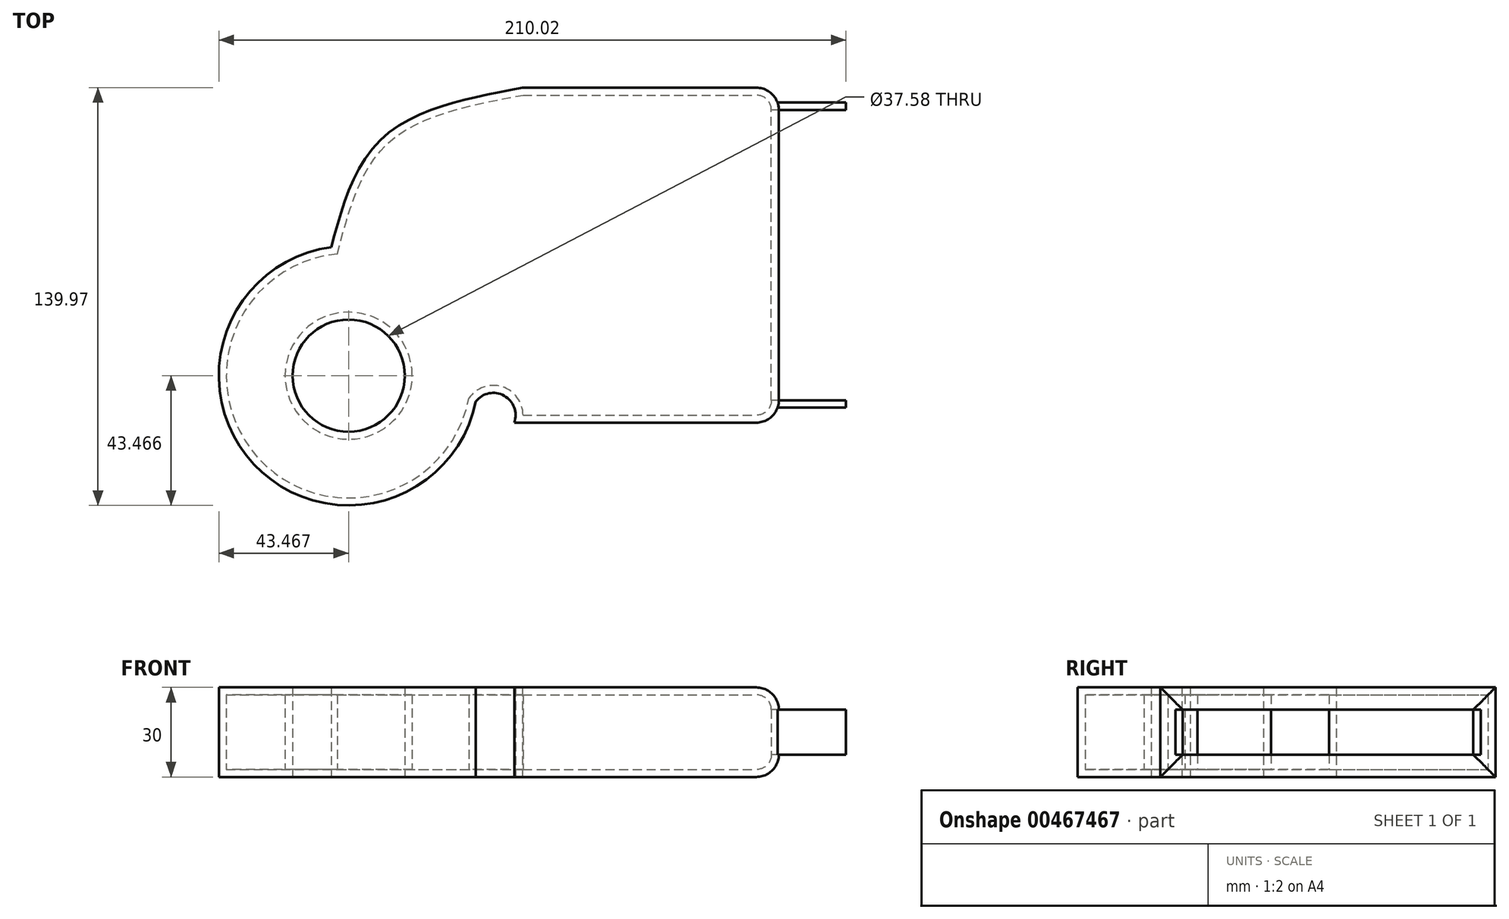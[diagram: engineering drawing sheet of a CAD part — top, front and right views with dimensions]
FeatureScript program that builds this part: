
annotation { "Feature Type Name" : "Feature", "Feature Type Description" : "" }
export const myFeature = defineFeature(function(context is Context, id is Id, definition is map)
    precondition{}
    {
        {
            var Q0;
            Q0=qCreatedBy(makeId("Top.planeOp"),FACE);
            var sketch = newSketch(context, id + "F0", { "sketchPlane" : qUnion([Q0])});
            skLineSegment(sketch, "E0.bottom", {"start": v(-39.88, -54.03) * mm, "end": v(43.27, -54.03) * mm});
            skLineSegment(sketch, "E0.top", {"start": v(-39.88, 53.2) * mm, "end": v(43.27, 53.2) * mm});
            skLineSegment(sketch, "E0.right", {"start": v(43.27, -54.03) * mm, "end": v(43.27, 53.2) * mm});
            skArc(sketch, "E1", {"start": v(-102.06, 0) * mm, "mid": v(-128.58, -68.38) * mm, "end": v(-58.02, -48.36) * mm});
            skArc(sketch, "E2", {"start": v(-39.88, -54.03) * mm, "mid": v(-46.87, -44.53) * mm, "end": v(-58.02, -48.36) * mm});
            skCircle(sketch, "E3", {"center": v(-98.28, -40.8) * mm, "radius": 21.29 * mm});
            skFitSpline(sketch, "E4", {"points": [v(-102.06, 0) * mm, v(-85.1, 37.1) * mm, v(-39.88, 53.2) * mm], "startDerivative": vector(22.98, 88.5) * mm, "endDerivative": vector(100.32, 18.86) * mm});
            skPoint(sketch, "E5", {"position": v(55.98, -27.17) * mm});
            skPoint(sketch, "E6", {"position": v(56.43, 31.28) * mm});
            skSolve(sketch);
        }
        {
            var Q0;
            Q0=makeQuery(id+"F0.imprint","IMPRINT",FACE,{"disambiguationData":[TD([[makeQuery(id+"F0.imprint","IMPRINT",EDGE,{"derivedFrom":sQuery(id+"F0.wireOp",EDGE,"E0.bottom")}),1.0]])]});
            extrude(context, id + "F1", {"entities" : qUnion([Q0]), "depth" : 25 * mm});
        }
        {
            var Q0;
            Q0=makeQuery(id+"F1.opExtrude","SWEPT_FACE",FACE,{"disambiguationData":[OSD([sQuery(id+"F0.wireOp",EDGE,"E0.right")])]});
            fillet(context, id + "F2", {"entities" : qUnion([Q0]), "radius" : 5 * mm, "tangentPropagation" : true, "allowEdgeOverflow" : false});
        }
        {
            var Q0;
            Q0=makeQuery(id+"F1.opExtrude","SWEPT_FACE",FACE,{"disambiguationData":[OSD([sQuery(id+"F0.wireOp",EDGE,"E0.right")])]});
            extrude(context, id + "F3", {"entities" : qUnion([Q0]), "operationType" : NewBodyOperationType.ADD, "depth" : 25 * mm});
        }
        {
            var Q0;
            Q0=makeQuery(id+"F3.opExtrude","CAP_FACE",FACE,{"disambiguationData":[OSD([sQuery(id+"F0.wireOp",EDGE,"E0.right")])],"isStart":false});
            var Q1;
            {var subQ0=sQuery(id+"F0.wireOp",EDGE,"E0.right");Q1=makeQuery(id+"F3.opExtrude","SWEPT_FACE",FACE,{"disambiguationData":[OSD([subQ0]),TDD([makeQuery(id+"F2.opFillet","BLEND_EDGE",EDGE,{"blendedFrom":[makeQuery(id+"F1.opExtrude","CAP_EDGE",EDGE,{"disambiguationData":[OSD([subQ0])],"isStart":false}),makeQuery(id+"F1.opExtrude","SWEPT_FACE",FACE,{"disambiguationData":[OSD([subQ0])]})],"blendedInto":[makeQuery(id+"F1.opExtrude","SWEPT_FACE",FACE,{"disambiguationData":[OSD([subQ0])]})]})])]});}
            var Q2;
            {var subQ0=sQuery(id+"F0.wireOp",EDGE,"E0.right");Q2=makeQuery(id+"F3.opExtrude","SWEPT_FACE",FACE,{"disambiguationData":[OSD([subQ0]),TDD([makeQuery(id+"F2.opFillet","BLEND_EDGE",EDGE,{"blendedFrom":[makeQuery(id+"F1.opExtrude","CAP_EDGE",EDGE,{"disambiguationData":[OSD([subQ0])],"isStart":true}),makeQuery(id+"F1.opExtrude","SWEPT_FACE",FACE,{"disambiguationData":[OSD([subQ0])]})],"blendedInto":[makeQuery(id+"F1.opExtrude","SWEPT_FACE",FACE,{"disambiguationData":[OSD([subQ0])]})]})])]});}
            shell(context, id + "F4", {"entities" : qUnion([Q0, Q1, Q2]), "thickness" : 2.5 * mm, "oppositeDirection" : true});
        }
    });
